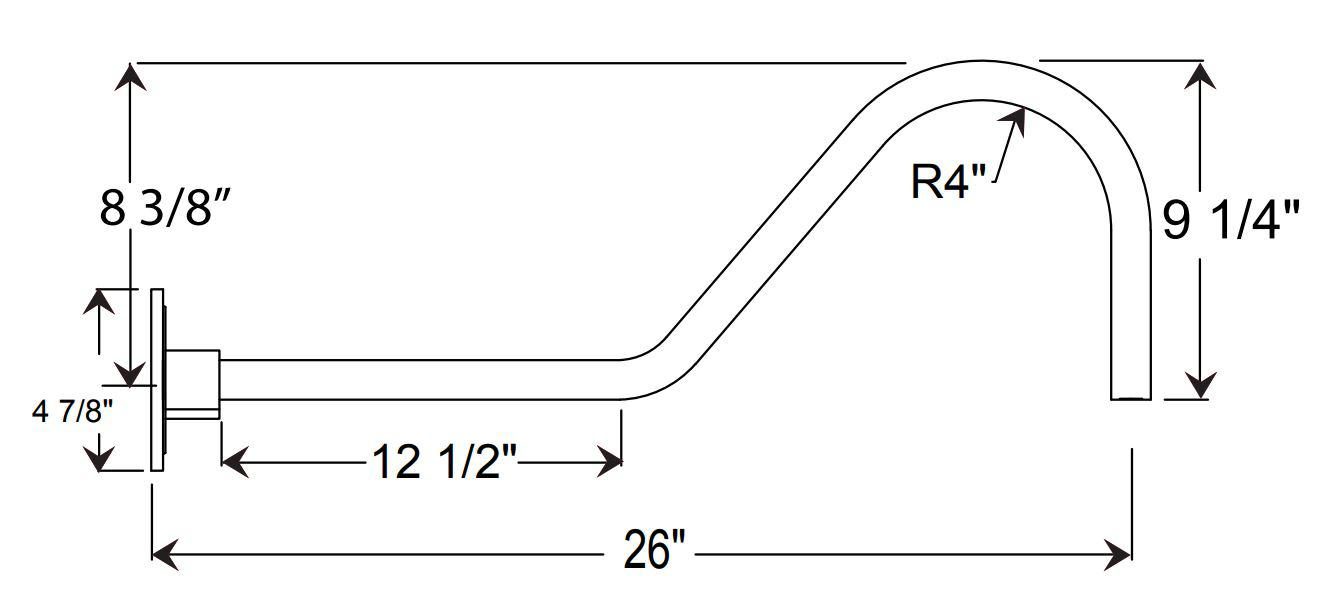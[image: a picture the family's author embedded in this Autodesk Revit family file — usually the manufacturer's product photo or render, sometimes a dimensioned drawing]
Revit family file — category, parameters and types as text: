
# Revit family: Orbitor 200w -16,18,20 MB
name_source: partatom
category: Lighting Fixtures
units: mm (PartAtom-declared; Revit-internal decimal feet)

## family parameters
Always vertical = Yes
Cut with Voids When Loaded = No
Light Source = Yes
OmniClass Number = 23.80.70.00
OmniClass Title = Lighting
Part Type = Normal
Room Calculation Point = No
Round Connector Dimension = Use Diameter
Shared = No
Work Plane-Based = No

## types (3) — shared parameters
Apparent Load = 200 VA
Body Colour = Spun aluminium
Body Material = body
CRI = >90
Color Filter = 16777215
Construction Material = Heavy Duty spun aluminum.
Default Elevation = 0' - 0"
Description = 120-277 Voltage
Dimming = 1%
Dimming Lamp Color Temperature Shift = <None>
Efficiency = 65-125 lumens per watt
INSIDE BODY = INSIDE BODY
Life = L70 50,000 hours
Load Classification = Lighting
Manufacturer = ANP Lighting
Power Factor = 1
Tilt Angle = 90.00°
URL = https://www.anplighting.com
Voltage = 277 V
Warranty = 5 year limited warranty
Wattage Comments = 200W Max

## per-type parameters (varying)
| type | Fixture Diameter | Fixture Height | Lamp | ORB216 | ORB218 | ORB220 | Photometric Web File | Weight |
| ORB216 | 1' - 4" | 1' - 0" | MB | Yes | No | No | ORB216CLM016LDDW40K.IES | 3.0 lbs |
| ORB218 | 1' - 6" | 1' - 1 1/2" | MB | No | Yes | No | ORB216CLM016LDDW40K.IES | 3.0 lbs |
| ORB220 | 1' - 8" | 1' - 2" | LED | No | No | Yes | ORB220CLM024LDDW40K.IES | 3.5 lbs |

note: column(s) folded — value = type name in every type: Model

## geometry (parser evidence)
native form markers: Sweep x23
no freeform markers — native parametric forms only
